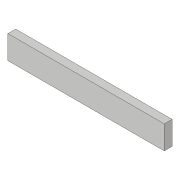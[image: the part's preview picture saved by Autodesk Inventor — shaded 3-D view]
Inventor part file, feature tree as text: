
AUTODESK INVENTOR PART (.ipt)
format: ipt  version: 2018 (Build 220112000, 112)  size: 75,264 bytes
history: native  units: in
note: dims shown in document units (in); Inventor stores cm internally (conversion verified against a paired STEP export)
features: extrude x1, sketch x1
ambient origin geometry x8: Origin, YZ Plane, XZ Plane, XY Plane, X Axis, Y Axis, Z Axis, Center Point
bodies: Solid1 (feature_tree)
feature tree (2):
  extrude  "Extrusion1"  TaperAngle=90.0deg  [1 undecoded]
  sketch  "Sketch1"  dims[d0=0.5906in d1=90.0deg d2=3.937in d3=90.0deg d4=0.5906in d5=90.0deg d6=0.1969in d7=0.0in]
note: 1 required parameter value undecoded (feature->parameter linkage not recoverable at this tier; creation-order binding heuristic only, values carry confidence <= 0.55)
